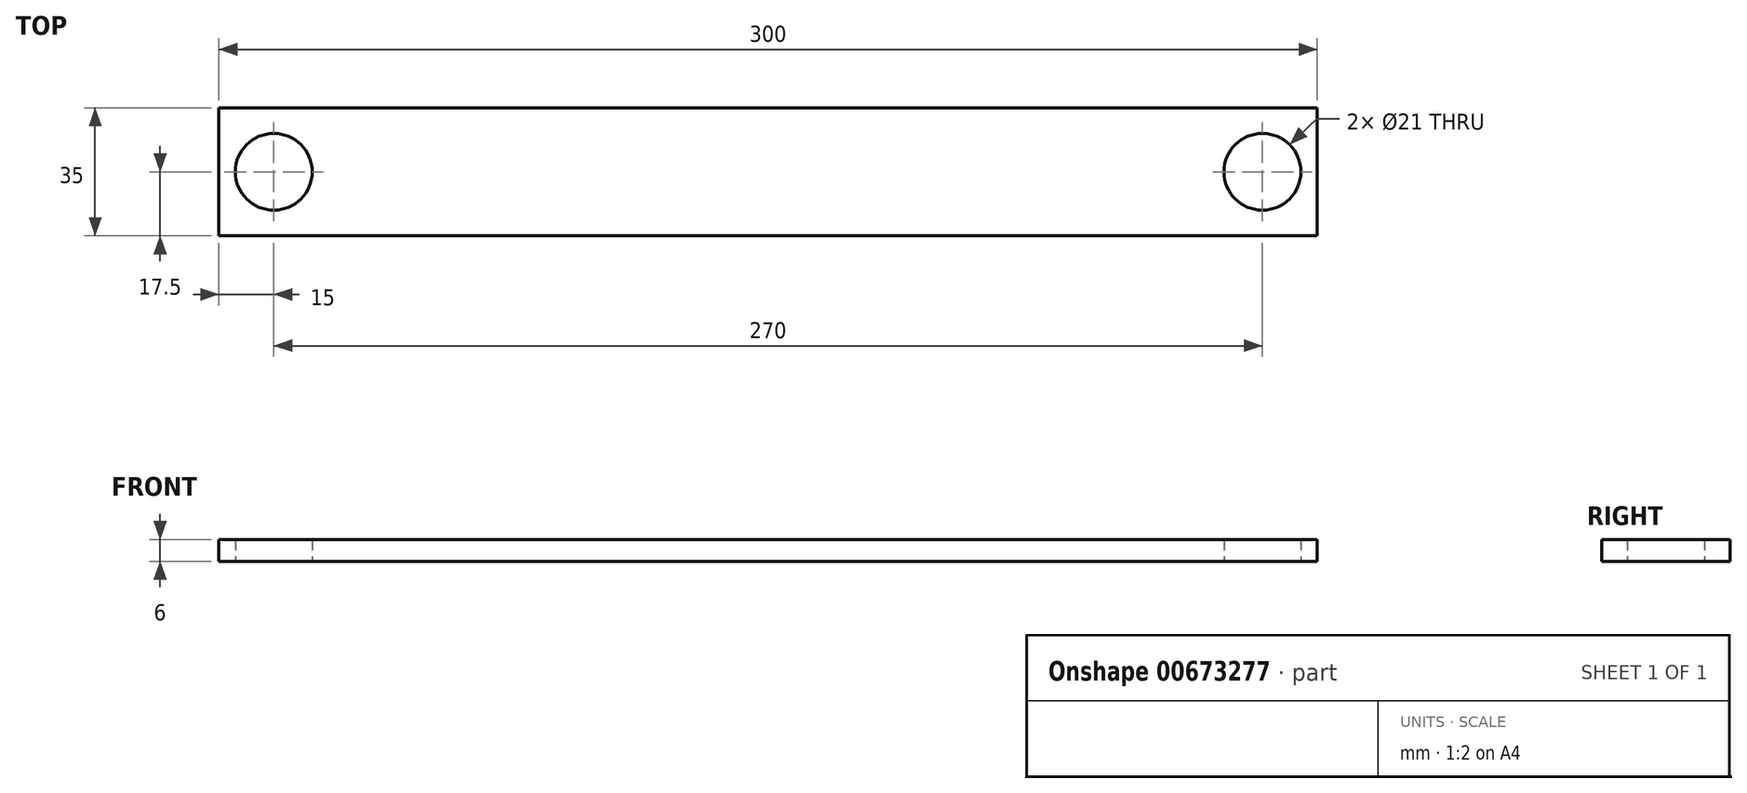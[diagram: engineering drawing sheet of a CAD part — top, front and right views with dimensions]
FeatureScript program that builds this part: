
annotation { "Feature Type Name" : "Feature", "Feature Type Description" : "" }
export const myFeature = defineFeature(function(context is Context, id is Id, definition is map)
    precondition{}
    {
        {
            var Q0;
            Q0=qCreatedBy(makeId("Top.planeOp"),FACE);
            var sketch = newSketch(context, id + "F0", { "sketchPlane" : qUnion([Q0])});
            skLineSegment(sketch, "E0.bottom", {"start": v(-150, 17.5) * mm, "end": v(150, 17.5) * mm});
            skLineSegment(sketch, "E0.top", {"start": v(-150, -17.5) * mm, "end": v(150, -17.5) * mm});
            skLineSegment(sketch, "E0.left", {"start": v(-150, 17.5) * mm, "end": v(-150, -17.5) * mm});
            skLineSegment(sketch, "E0.right", {"start": v(150, 17.5) * mm, "end": v(150, -17.5) * mm});
            skCircle(sketch, "E1", {"center": v(-135, 0) * mm, "radius": 10.5 * mm});
            skCircle(sketch, "E2", {"center": v(135, 0) * mm, "radius": 10.5 * mm});
            skLineSegment(sketch, "E3", {"start": v(0, 17.5) * mm, "end": v(0, -17.5) * mm, "construction": true});
            skLineSegment(sketch, "E4", {"start": v(150, 0) * mm, "end": v(-150, 0) * mm, "construction": true});
            skSolve(sketch);
        }
        {
            var Q0;
            Q0=makeQuery(id+"F0.imprint","IMPRINT",FACE,{"disambiguationData":[TD([[makeQuery(id+"F0.imprint","IMPRINT",EDGE,{"derivedFrom":sQuery(id+"F0.wireOp",EDGE,"E0.bottom")}),-1.0]])]});
            extrude(context, id + "F1", {"entities" : qUnion([Q0]), "depth" : 6 * mm, "offsetDistance" : 25 * mm});
        }
    });
